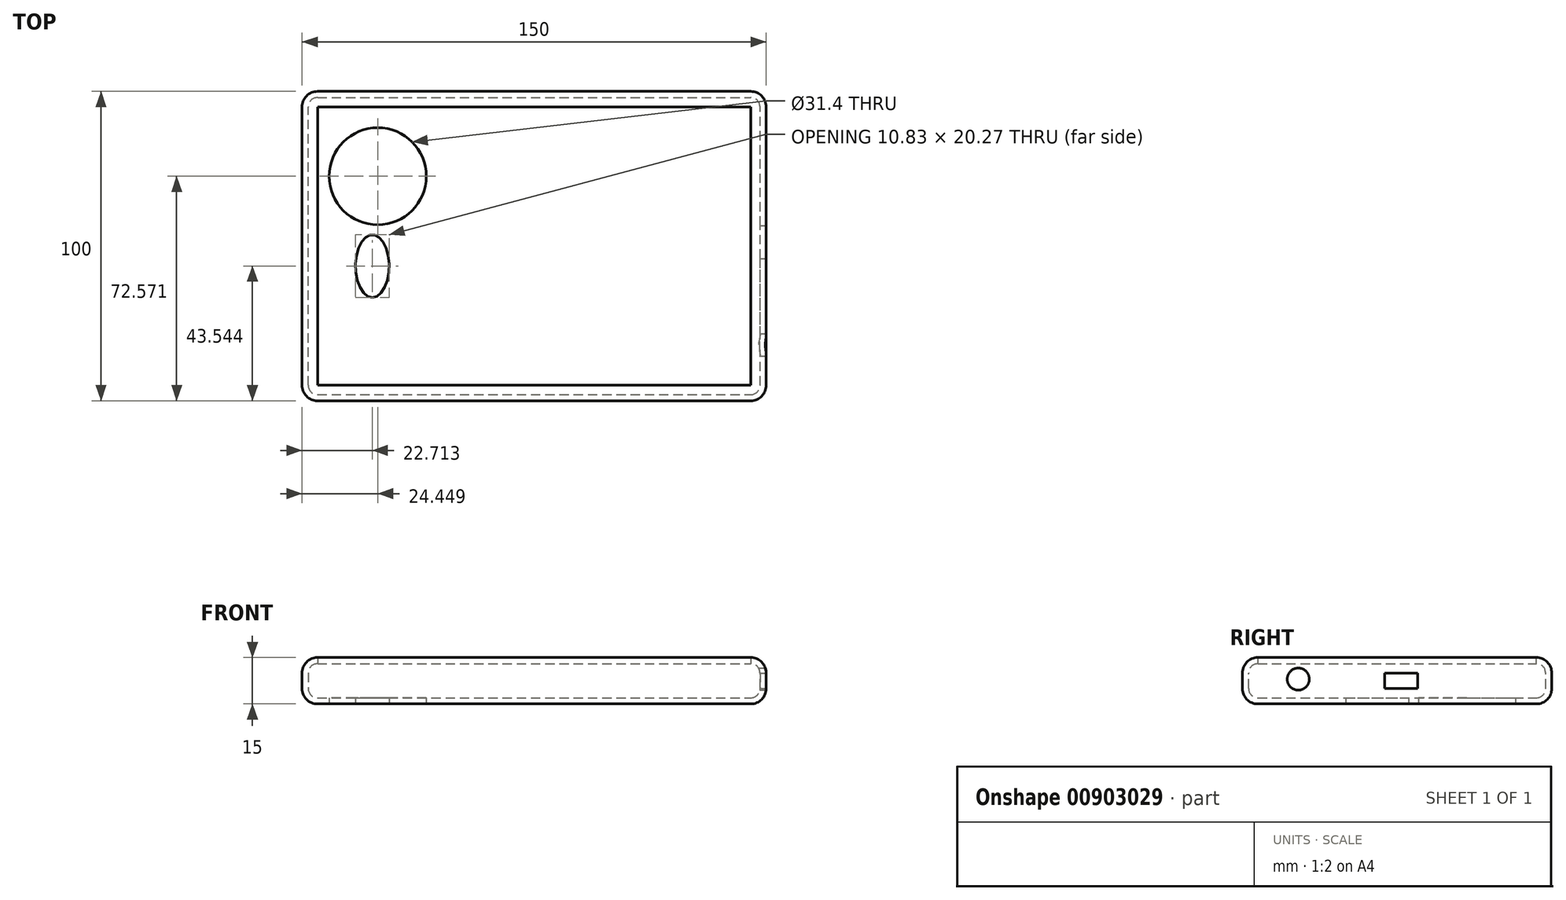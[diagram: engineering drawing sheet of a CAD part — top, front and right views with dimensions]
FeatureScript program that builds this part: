
annotation { "Feature Type Name" : "Feature", "Feature Type Description" : "" }
export const myFeature = defineFeature(function(context is Context, id is Id, definition is map)
    precondition{}
    {
        {
            var Q0;
            Q0=qCreatedBy(makeId("Top.planeOp"),FACE);
            var sketch = newSketch(context, id + "F0", { "sketchPlane" : qUnion([Q0])});
            skLineSegment(sketch, "E0.bottom", {"start": v(-75, 50) * mm, "end": v(75, 50) * mm});
            skLineSegment(sketch, "E0.top", {"start": v(-75, -50) * mm, "end": v(75, -50) * mm});
            skLineSegment(sketch, "E0.left", {"start": v(-75, 50) * mm, "end": v(-75, -50) * mm});
            skLineSegment(sketch, "E0.right", {"start": v(75, 50) * mm, "end": v(75, -50) * mm});
            skPoint(sketch, "E0.middle", {"position": v(0, 0) * mm});
            skSolve(sketch);
        }
        {
            var Q0;
            Q0 = qSketchRegion(id + "F0", true);
            extrude(context, id + "F1", {"entities" : qUnion([Q0]), "depth" : 15 * mm, "offsetDistance" : 25 * mm});
        }
        {
            var Q0;
            Q0=makeQuery(id+"F1.opExtrude","SWEPT_EDGE",EDGE,{"disambiguationData":[OSD([sQuery(id+"F0.wireOp",EDGE,"E0.bottom"),sQuery(id+"F0.wireOp",EDGE,"E0.left")])]});
            var Q1;
            Q1=makeQuery(id+"F1.opExtrude","SWEPT_EDGE",EDGE,{"disambiguationData":[OSD([sQuery(id+"F0.wireOp",EDGE,"E0.top"),sQuery(id+"F0.wireOp",EDGE,"E0.left")])]});
            var Q2;
            Q2=makeQuery(id+"F1.opExtrude","SWEPT_EDGE",EDGE,{"disambiguationData":[OSD([sQuery(id+"F0.wireOp",EDGE,"E0.top"),sQuery(id+"F0.wireOp",EDGE,"E0.right")])]});
            var Q3;
            Q3=makeQuery(id+"F1.opExtrude","CAP_EDGE",EDGE,{"disambiguationData":[OSD([sQuery(id+"F0.wireOp",EDGE,"E0.bottom")])],"isStart":true});
            var Q4;
            Q4=makeQuery(id+"F1.opExtrude","CAP_EDGE",EDGE,{"disambiguationData":[OSD([sQuery(id+"F0.wireOp",EDGE,"E0.top")])],"isStart":true});
            var Q5;
            Q5=makeQuery(id+"F1.opExtrude","CAP_EDGE",EDGE,{"disambiguationData":[OSD([sQuery(id+"F0.wireOp",EDGE,"E0.top")])],"isStart":false});
            var Q6;
            Q6=makeQuery(id+"F1.opExtrude","CAP_EDGE",EDGE,{"disambiguationData":[OSD([sQuery(id+"F0.wireOp",EDGE,"E0.left")])],"isStart":true});
            var Q7;
            Q7=makeQuery(id+"F1.opExtrude","CAP_EDGE",EDGE,{"disambiguationData":[OSD([sQuery(id+"F0.wireOp",EDGE,"E0.left")])],"isStart":false});
            var Q8;
            Q8=makeQuery(id+"F1.opExtrude","CAP_EDGE",EDGE,{"disambiguationData":[OSD([sQuery(id+"F0.wireOp",EDGE,"E0.right")])],"isStart":true});
            var Q9;
            Q9=makeQuery(id+"F1.opExtrude","CAP_EDGE",EDGE,{"disambiguationData":[OSD([sQuery(id+"F0.wireOp",EDGE,"E0.bottom")])],"isStart":false});
            var Q10;
            Q10=makeQuery(id+"F1.opExtrude","CAP_EDGE",EDGE,{"disambiguationData":[OSD([sQuery(id+"F0.wireOp",EDGE,"E0.right")])],"isStart":false});
            fillet(context, id + "F2", {"entities" : qUnion([Q0, Q1, Q2, Q3, Q4, Q5, Q6, Q7, Q8, Q9, Q10]), "radius" : 5 * mm, "tangentPropagation" : true, "allowEdgeOverflow" : false});
        }
        {
            var Q0;
            Q0=makeQuery(id+"F1.opExtrude","SWEPT_EDGE",EDGE,{"disambiguationData":[OSD([sQuery(id+"F0.wireOp",EDGE,"E0.bottom"),sQuery(id+"F0.wireOp",EDGE,"E0.right")])]});
            fillet(context, id + "F3", {"entities" : qUnion([Q0]), "radius" : 5 * mm, "tangentPropagation" : true, "allowEdgeOverflow" : false});
        }
        {
            var Q0;
            Q0=makeQuery(id+"F1.opExtrude","CAP_FACE",FACE,{"disambiguationData":[OSD([sQuery(id+"F0.wireOp",EDGE,"E0.bottom"),sQuery(id+"F0.wireOp",EDGE,"E0.top"),sQuery(id+"F0.wireOp",EDGE,"E0.left"),sQuery(id+"F0.wireOp",EDGE,"E0.right")])],"isStart":false});
            shell(context, id + "F4", {"entities" : qUnion([Q0]), "thickness" : 2 * mm});
        }
        {
            var Q0;
            Q0=makeQuery(id+"F1.opExtrude","CAP_FACE",FACE,{"disambiguationData":[OSD([sQuery(id+"F0.wireOp",EDGE,"E0.bottom"),sQuery(id+"F0.wireOp",EDGE,"E0.top"),sQuery(id+"F0.wireOp",EDGE,"E0.left"),sQuery(id+"F0.wireOp",EDGE,"E0.right")])],"isStart":true});
            var sketch = newSketch(context, id + "F5", { "sketchPlane" : qUnion([Q0])});
            skSolve(sketch);
        }
        {
            var Q0;
            {var subQ0=sQuery(id+"F0.wireOp",EDGE,"E0.right");var subQ1=sQuery(id+"F0.wireOp",EDGE,"E0.left");var subQ2=sQuery(id+"F0.wireOp",EDGE,"E0.top");var subQ3=sQuery(id+"F0.wireOp",EDGE,"E0.bottom");var subQ4=makeQuery(id+"F1.opExtrude","CAP_FACE",FACE,{"disambiguationData":[OSD([subQ3,subQ2,subQ1,subQ0])],"isStart":true});Q0=makeQuery(id+"F5.imprint","IMPRINT",FACE,{"disambiguationData":[TD([[makeQuery(id+"F5.imprint","IMPRINT",EDGE,{"derivedFrom":makeQuery(id+"F2.opFillet","BLEND_EDGE",EDGE,{"blendedFrom":[makeQuery(id+"F1.opExtrude","CAP_EDGE",EDGE,{"disambiguationData":[OSD([subQ3])],"isStart":true}),subQ4],"blendedInto":[subQ4]})}),1.0]])]});}
            var sketch = newSketch(context, id + "F6", { "sketchPlane" : qUnion([Q0])});
            skCircle(sketch, "E1", {"center": v(-50.55, -22.57) * mm, "radius": 15.7 * mm});
            skEllipse(sketch, "E2", {"center": v(-52.29, 6.46) * mm, "majorRadius": 10.14 * mm, "minorRadius": 5.42 * mm, "majorAxis": v(0, 1)});
            skSolve(sketch);
        }
        {
            var Q0;
            Q0 = qSketchRegion(id + "F6", true);
            extrude(context, id + "F7", {"entities" : qUnion([Q0]), "operationType" : NewBodyOperationType.REMOVE, "oppositeDirection" : true, "depth" : 25 * mm, "offsetDistance" : 25 * mm});
        }
        {
            var Q0;
            Q0=makeQuery(id+"F1.opExtrude","SWEPT_FACE",FACE,{"disambiguationData":[OSD([sQuery(id+"F0.wireOp",EDGE,"E0.right")])]});
            var sketch = newSketch(context, id + "F8", { "sketchPlane" : qUnion([Q0])});
            skLineSegment(sketch, "E3.bottom", {"start": v(-4, 10) * mm, "end": v(6.63, 10) * mm});
            skLineSegment(sketch, "E3.top", {"start": v(-4, 5) * mm, "end": v(6.63, 5) * mm});
            skLineSegment(sketch, "E3.left", {"start": v(-4, 10) * mm, "end": v(-4, 5) * mm});
            skLineSegment(sketch, "E3.right", {"start": v(6.63, 10) * mm, "end": v(6.63, 5) * mm});
            skCircle(sketch, "E4", {"center": v(-31.93, 8.03) * mm, "radius": 3.57 * mm});
            skSolve(sketch);
        }
        {
            var Q0;
            Q0 = qSketchRegion(id + "F8", true);
            extrude(context, id + "F9", {"entities" : qUnion([Q0]), "operationType" : NewBodyOperationType.REMOVE, "oppositeDirection" : true, "depth" : 25 * mm, "offsetDistance" : 25 * mm});
        }
    });
